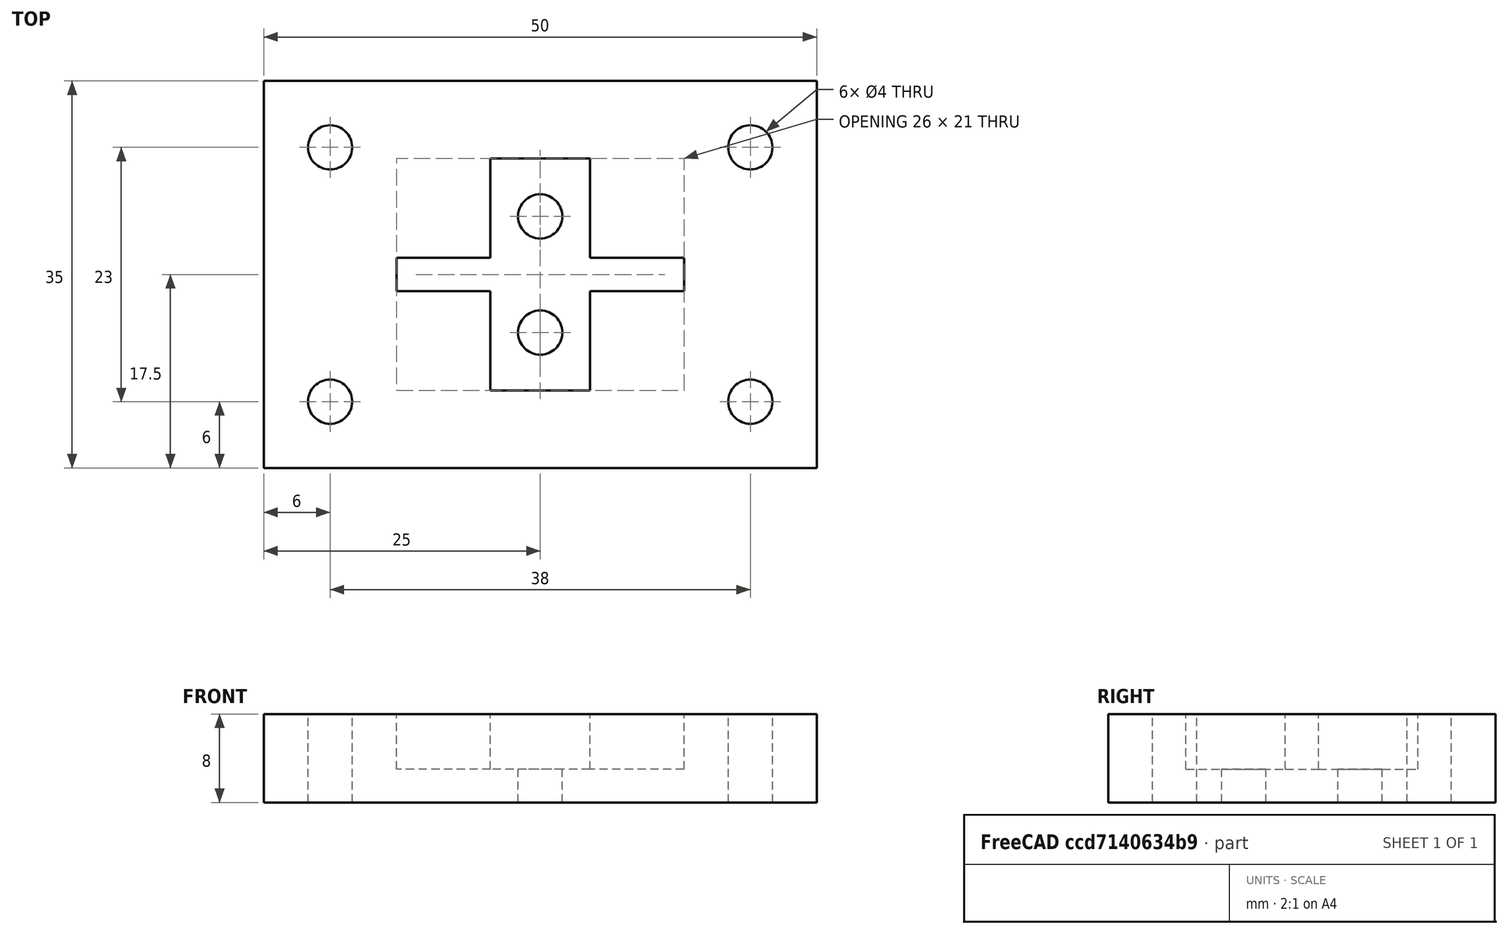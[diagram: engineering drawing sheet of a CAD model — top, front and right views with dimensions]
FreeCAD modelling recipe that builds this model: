
FCSTD DOCUMENT  (FreeCAD 0.17R13541 (Git))
Label: SolenoidHolder
License: All rights reserved
LicenseURL: http://en.wikipedia.org/wiki/All_rights_reserved
objects: Part::Cut×8, Part::Cylinder×6, Part::Box×4, Part::MultiFuse×1
note: 19 computed .brp shape members not serialized (recipe doc carries the construction recipe); baked Part::Feature solids carry a one-line shape summary decoded from their .brp

FEATURE [Part::Box] Box  label="Cube"
  AttacherType = Attacher::AttachEngine3D
  Height = 8
  Length = 50
  Width = 35
FEATURE [Part::Box] Box001  label="Cube001"
  AttacherType = Attacher::AttachEngine3D
  Height = 8
  Length = 26
  Placement = pos=(12,16,0) rot=(0,0,1;0rad)
  Width = 3
FEATURE [Part::Box] Box002  label="Cube002"
  AttacherType = Attacher::AttachEngine3D
  Height = 8
  Length = 9
  Placement = pos=(20.5,7,0) rot=(0,0,1;0rad)
  Width = 21
FEATURE [Part::Cut] Cut
  Base = -> Box
  Tool = -> Box002
FEATURE [Part::Cylinder] Cylinder
  Angle = 360
  AttacherType = Attacher::AttachEngine3D
  Height = 10
  Placement = pos=(6,6,0) rot=(0,0,1;0rad)
  Radius = 2
FEATURE [Part::Cylinder] Cylinder001
  Angle = 360
  AttacherType = Attacher::AttachEngine3D
  Height = 10
  Placement = pos=(44,6,0) rot=(0,0,1;0rad)
  Radius = 2
FEATURE [Part::Cylinder] Cylinder002
  Angle = 360
  AttacherType = Attacher::AttachEngine3D
  Height = 10
  Placement = pos=(6,29,0) rot=(0,0,1;0rad)
  Radius = 2
FEATURE [Part::Cylinder] Cylinder003
  Angle = 360
  AttacherType = Attacher::AttachEngine3D
  Height = 10
  Placement = pos=(44,29,0) rot=(0,0,1;0rad)
  Radius = 2
FEATURE [Part::Box] Box003  label="Cube003"
  AttacherType = Attacher::AttachEngine3D
  Height = 3
  Length = 50
  Width = 35
FEATURE [Part::Cylinder] Cylinder004
  Angle = 360
  AttacherType = Attacher::AttachEngine3D
  Height = 10
  Placement = pos=(25,22.755,0) rot=(0,0,1;0rad)
  Radius = 2
FEATURE [Part::Cylinder] Cylinder005
  Angle = 360
  AttacherType = Attacher::AttachEngine3D
  Height = 10
  Placement = pos=(25,12.25,0) rot=(0,0,1;0rad)
  Radius = 2
FEATURE [Part::Cut] Cut001
  Base = -> Box003
  Tool = -> Cylinder005
FEATURE [Part::Cut] Cut002
  Base = -> Cut001
  Tool = -> Cylinder004
FEATURE [Part::Cut] Cut003
  Base = -> Cut
  Tool = -> Box001
FEATURE [Part::MultiFuse] Fusion
  Shapes = -> [Cut002,Cut003]
FEATURE [Part::Cut] Cut004
  Base = -> Fusion
  Tool = -> Cylinder
FEATURE [Part::Cut] Cut005
  Base = -> Cut004
  Tool = -> Cylinder001
FEATURE [Part::Cut] Cut006
  Base = -> Cut005
  Tool = -> Cylinder002
FEATURE [Part::Cut] Cut007
  Base = -> Cut006
  Tool = -> Cylinder003
